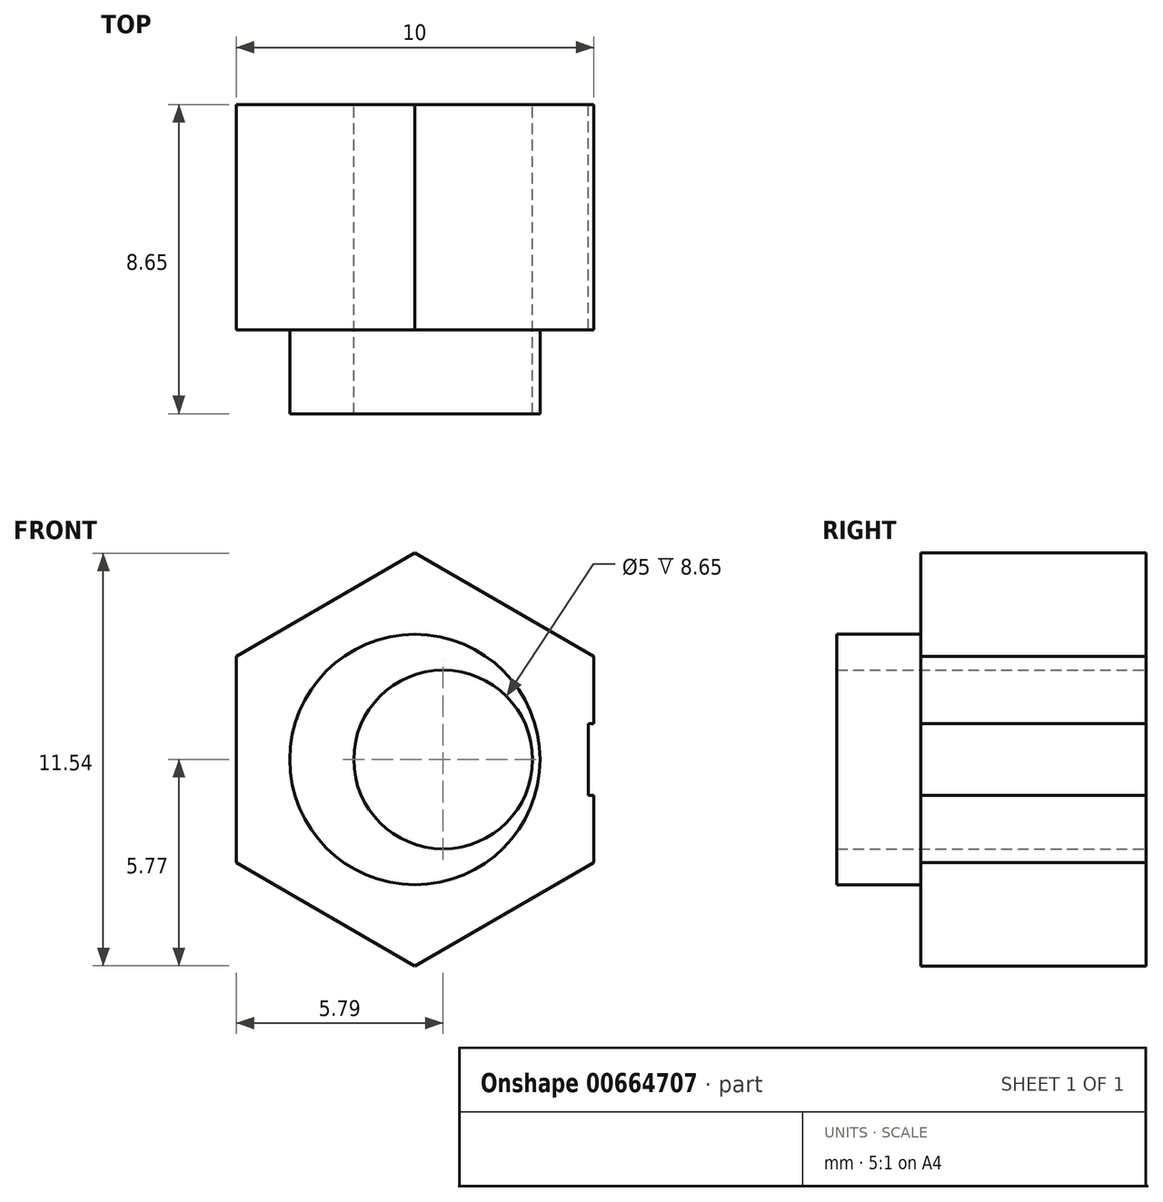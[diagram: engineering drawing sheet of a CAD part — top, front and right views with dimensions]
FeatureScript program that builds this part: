
annotation { "Feature Type Name" : "Feature", "Feature Type Description" : "" }
export const myFeature = defineFeature(function(context is Context, id is Id, definition is map)
    precondition{}
    {
        {
            var Q0;
            Q0=qCreatedBy(makeId("Front.planeOp"),FACE);
            var sketch = newSketch(context, id + "F0", { "sketchPlane" : qUnion([Q0])});
            skCircle(sketch, "E0.cCircle", {"center": v(0, 0) * mm, "radius": 5 * mm, "construction": true});
            skLineSegment(sketch, "E0.0", {"start": v(5, 2.89) * mm, "end": v(5, -2.89) * mm});
            skLineSegment(sketch, "E0.1", {"start": v(5, -2.89) * mm, "end": v(0, -5.77) * mm});
            skLineSegment(sketch, "E0.2", {"start": v(0, -5.77) * mm, "end": v(-5, -2.89) * mm});
            skLineSegment(sketch, "E0.3", {"start": v(-5, -2.89) * mm, "end": v(-5, 2.89) * mm});
            skLineSegment(sketch, "E0.4", {"start": v(-5, 2.89) * mm, "end": v(0, 5.77) * mm});
            skLineSegment(sketch, "E0.5", {"start": v(0, 5.77) * mm, "end": v(5, 2.89) * mm});
            skPoint(sketch, "E0.0.midPoint", {"position": v(5, 0) * mm});
            skLineSegment(sketch, "E1", {"start": v(0, -8.67) * mm, "end": v(0, 8.78) * mm, "construction": true});
            skLineSegment(sketch, "E2.0", {"start": v(0.79, -8.67) * mm, "end": v(0.79, 8.78) * mm, "construction": true});
            skCircle(sketch, "E3", {"center": v(0.79, 0) * mm, "radius": 2.5 * mm});
            skLineSegment(sketch, "E4", {"start": v(5, 0) * mm, "end": v(4.85, 0) * mm, "construction": true});
            skLineSegment(sketch, "E5.0", {"start": v(5, 1) * mm, "end": v(4.85, 1) * mm, "construction": true});
            skLineSegment(sketch, "E6.0", {"start": v(5, -1) * mm, "end": v(4.85, -1) * mm, "construction": true});
            skLineSegment(sketch, "E7", {"start": v(5, -1) * mm, "end": v(4.85, -1) * mm});
            skLineSegment(sketch, "E8", {"start": v(4.85, 1) * mm, "end": v(4.85, -1) * mm});
            skLineSegment(sketch, "E9", {"start": v(4.85, 1) * mm, "end": v(5, 1) * mm});
            skLineSegment(sketch, "E10", {"start": v(5, 1) * mm, "end": v(5, -1) * mm});
            skSolve(sketch);
        }
        {
            var Q0;
            Q0=makeQuery(id+"F0.imprint","IMPRINT",FACE,{"disambiguationData":[TD([[makeQuery(id+"F0.imprint","IMPRINT",EDGE,{"derivedFrom":sQuery(id+"F0.wireOp",EDGE,"E0.0")}),-1.0]])]});
            var Q1;
            Q1=makeQuery(id+"F0.imprint","IMPRINT",FACE,{"disambiguationData":[TD([[makeQuery(id+"F0.imprint","IMPRINT",EDGE,{"derivedFrom":sQuery(id+"F0.wireOp",EDGE,"sGghlq6r-cmlH-7LTg-aPMt-5TyCXqs2uNgx")}),1.0]])]});
            extrude(context, id + "F1", {"entities" : qUnion([Q0, Q1]), "depth" : 6.3 * mm, "offsetDistance" : 25 * mm});
        }
        {
            var Q0;
            Q0=makeQuery(id+"F1.opExtrude","CAP_FACE",FACE,{"disambiguationData":[OSD([sQuery(id+"F0.wireOp",EDGE,"E0.0"),sQuery(id+"F0.wireOp",EDGE,"E0.1"),sQuery(id+"F0.wireOp",EDGE,"E0.2"),sQuery(id+"F0.wireOp",EDGE,"E0.3"),sQuery(id+"F0.wireOp",EDGE,"E0.4"),sQuery(id+"F0.wireOp",EDGE,"E0.5"),sQuery(id+"F0.wireOp",EDGE,"CpPwzaqu-h3LP-73l1-ozuF-M9ZyCNbdTlve")])],"isStart":false});
            cPlane(context, id + "F2", {"entities" : qUnion([Q0]), "cplaneType" : CPlaneType.OFFSET, "offset" : 0 * mm, "width" : 150 * mm, "height" : 150 * mm});
        }
        {
            var Q0;
            Q0=qCreatedBy(id+"F2.planeOp",FACE);
            var sketch = newSketch(context, id + "F3", { "sketchPlane" : qUnion([Q0])});
            skCircle(sketch, "E11", {"center": v(0, 0) * mm, "radius": 3.5 * mm});
            skSolve(sketch);
        }
        {
            var Q0;
            Q0=makeQuery(id+"F3.imprint","IMPRINT",FACE,{"disambiguationData":[TD([[makeQuery(id+"F3.imprint","IMPRINT",EDGE,{"derivedFrom":sQuery(id+"F3.wireOp",EDGE,"E11")}),1.0]])]});
            extrude(context, id + "F4", {"entities" : qUnion([Q0]), "operationType" : NewBodyOperationType.ADD, "depth" : 2.35 * mm, "offsetDistance" : 25 * mm});
        }
        {
            var Q0;
            Q0=makeQuery(id+"F0.imprint","IMPRINT",FACE,{"disambiguationData":[TD([[makeQuery(id+"F0.imprint","IMPRINT",EDGE,{"derivedFrom":sQuery(id+"F0.wireOp",EDGE,"E3")}),1.0]])]});
            var Q1;
            Q1=makeQuery(id+"F4.opExtrude","CAP_FACE",FACE,{"disambiguationData":[OSD([sQuery(id+"F3.wireOp",EDGE,"E11")])],"isStart":false});
            extrude(context, id + "F5", {"entities" : qUnion([Q0]), "operationType" : NewBodyOperationType.REMOVE, "endBound" : BoundingType.UP_TO_SURFACE, "depth" : 25 * mm, "endBoundEntityFace" : qUnion([Q1]), "offsetDistance" : 25 * mm});
        }
        {
            var Q0;
            Q0=qCreatedBy(makeId("Top.planeOp"),FACE);
            var sketch = newSketch(context, id + "F6", { "sketchPlane" : qUnion([Q0])});
            skLineSegment(sketch, "E12", {"start": v(-5, -6.3) * mm, "end": v(-6.1, -6.3) * mm});
            skLineSegment(sketch, "E13", {"start": v(-6.1, -6.3) * mm, "end": v(-6.1, -6.6) * mm});
            skLineSegment(sketch, "E14", {"start": v(-6.1, -6.6) * mm, "end": v(-5, -6.3) * mm});
            skLineSegment(sketch, "E15", {"start": v(0, 0) * mm, "end": v(0, -13.07) * mm, "construction": true});
            skSolve(sketch);
        }
        {
            var Q0;
            Q0=makeQuery(id+"F6.imprint","IMPRINT",FACE,{"disambiguationData":[TD([[makeQuery(id+"F6.imprint","IMPRINT",EDGE,{"derivedFrom":sQuery(id+"F6.wireOp",EDGE,"E12")}),1.0]])]});
            var Q1;
            Q1=sQuery(id+"F6.wireOp",EDGE,"E15");
            revolve(context, id + "F7", {"operationType" : NewBodyOperationType.REMOVE, "entities" : qUnion([Q0]), "axis" : qUnion([Q1]), "revolveType" : RevolveType.FULL, "oppositeDirection" : true});
        }
        {
            var Q0;
            Q0=makeQuery(id+"F0.imprint","IMPRINT",FACE,{"disambiguationData":[TD([[makeQuery(id+"F0.imprint","IMPRINT",EDGE,{"derivedFrom":sQuery(id+"F0.wireOp",EDGE,"E7")}),-1.0]])]});
            extrude(context, id + "F8", {"entities" : qUnion([Q0]), "operationType" : NewBodyOperationType.REMOVE, "endBound" : BoundingType.THROUGH_ALL, "oppositeDirection" : true, "depth" : 25 * mm, "offsetDistance" : 25 * mm});
        }
    });
